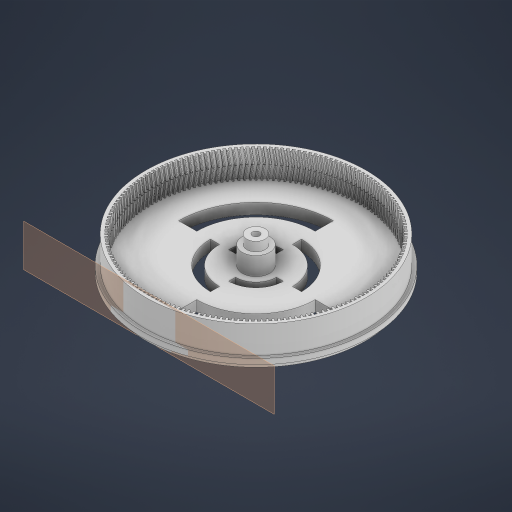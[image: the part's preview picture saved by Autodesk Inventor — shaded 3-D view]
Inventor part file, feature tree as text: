
AUTODESK INVENTOR PART (.ipt)
format: ipt  version: 2023 (Build 270158030, 158C)  size: 2,458,624 bytes
history: native  units: in
note: dims shown in document units (in); Inventor stores cm internally (conversion verified against a paired STEP export)
features: extrude x10, sketch x8, plane x1, fillet x1, pattern_circular x1
ambient origin geometry x8: Origin, YZ Plane, XZ Plane, XY Plane, X Axis, Y Axis, Z Axis, Center Point
bodies: Solid1 (feature_tree)
feature tree (21):
  extrude  "Extrusion1"  Depth=0.2362in TaperAngle=0.0deg
  extrude  "Extrusion2"  Depth=0.2362in TaperAngle=0.0deg
  extrude  "Extrusion3"  Depth=0.315in TaperAngle=0.0deg
  extrude  "Extrusion5"  Depth=1.1811in
  extrude  "Extrusion6"  Depth=1.1811in
  plane  "Work Plane2"
  extrude  "Extrusion8"  Depth=0.0787in
  fillet  "Fillet1"  Radius=0.0787in
  sketch  "Sketch26"  dims[d28=0.1181in d29=0.0in d38=0.0394in]
  extrude  "Extrusion11"  Depth=0.0394in
  extrude  "Extrusion12"  Depth=1.1811in
  extrude  "Extrusion13"  Depth=1.1811in
  pattern_circular  "Circular Pattern3"  Count=2  [1 undecoded]
  extrude  "Extrusion15"  Depth=1.1811in TaperAngle=0.0deg
  sketch  "Sketch2"  dims[d0=9.8425in d1=0.2362in d2=0.0in]
  sketch  "Sketch3"  dims[d3=9.4488in d4=0.2362in d5=0.0in]
  sketch  "Sketch4"  dims[d6=0.315in d7=0.315in d8=0.0in]
  sketch  "Sketch9"  dims[d15=1.1811in d16=0.0in d17=9.252in]
  sketch  "Sketch12"  dims[d18=1.1811in d19=0.0in d24=4.626in]
  sketch  "Sketch17"  dims[d25=0.0787in d26=0.0787in d27=0.0787in]
  sketch  "Sketch28"  dims[d42=1.1811in d43=0.7874in d44=0.3071in d45=0.7874in d46=0.0in d47=1.1811in d48=0.0in d49=0.0in d50=0.0in d51=63.7795in d52=360.0deg d61=1.7717in d62=2.3622in d63=3.1496in d64=3.937in d65=5.1181in d66=6.6929in d67=0.5906in d68=0.0in]
note: 1 required parameter value undecoded (feature->parameter linkage not recoverable at this tier; creation-order binding heuristic only, values carry confidence <= 0.55)
